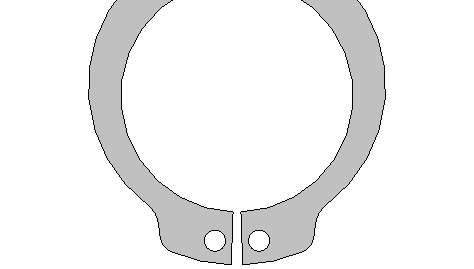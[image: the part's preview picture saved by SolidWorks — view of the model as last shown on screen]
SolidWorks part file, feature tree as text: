
SOLIDWORKS PART (.sldprt)
format: sldprt  version: not decoded by parser v0  size: 168,448 bytes
history: native  units: mm
features: cut_extrude x4, plane x3, sketch x3, material x1, extrude x1 (+8 scaffold rows collapsed)
feature tree (20):
  scaffold x8  (default folders/planes/origin — collapsed)
  material  "Matériau <non spécifié>"
  plane  "Plane1"
  plane  "Plane2"
  plane  "Plane3"
  sketch  "Clipboard"  dims[HoleDia=1.2mm ShaftDia=14.0mm LargeSection=2.4mm SmallSection=1.4mm LugSection=3.0mm]
  sketch  "BodySke"  dims[c1.GrooveDia=13.15mm c1.OutsideDia=~4.355353mm c1.TipRad=~0.23622mm c1.D3=2.6924mm c1.LugRad=9.575mm c1.HoleOffsetRad=8.2875mm c1.HoleDia=1.2mm c2.D3=1.0mm c2.CavityRad=~1.532653mm c2.CavityWidth=3.0861mm c2.D1=~5.632972mm c3.D1=10.0deg c3.D2=~1.961375mm c4.D2=15.0deg c4.LargeRad=8.975mm c4.SmallRad=7.975mm c4.Gap=0.4445mm c4.D1=7.239mm c4.SmallAngle=~78.075027deg c5.D2=~3.638241mm c6.D2=15.0deg c6.HoleSpacing=2.5mm c6.Gap=0.4445mm c6.D1=2.5654mm c7.D1=~3.518715deg c7.Gap=0.65mm]
  extrude  "Body"  Depth=1.3mm Thickness=1.3mm
  sketch  "NotSke"
  cut_extrude  "Notch"  [1 undecoded]
  cut_extrude  "ConfigurationName"  Depth=0 CopiedFlag=0
  cut_extrude  "PartNumberID"  [1 undecoded]
  cut_extrude  "ConfigurationName"  Depth=0 CopiedFlag=0
decode coverage: 5 of 8 modeling features carry decoded parameters
note: ~ marks probable driven/reference dimensions
note: 2 parameter values undecoded
note: suppression state not decoded; provenance and decode notes live in map.json
